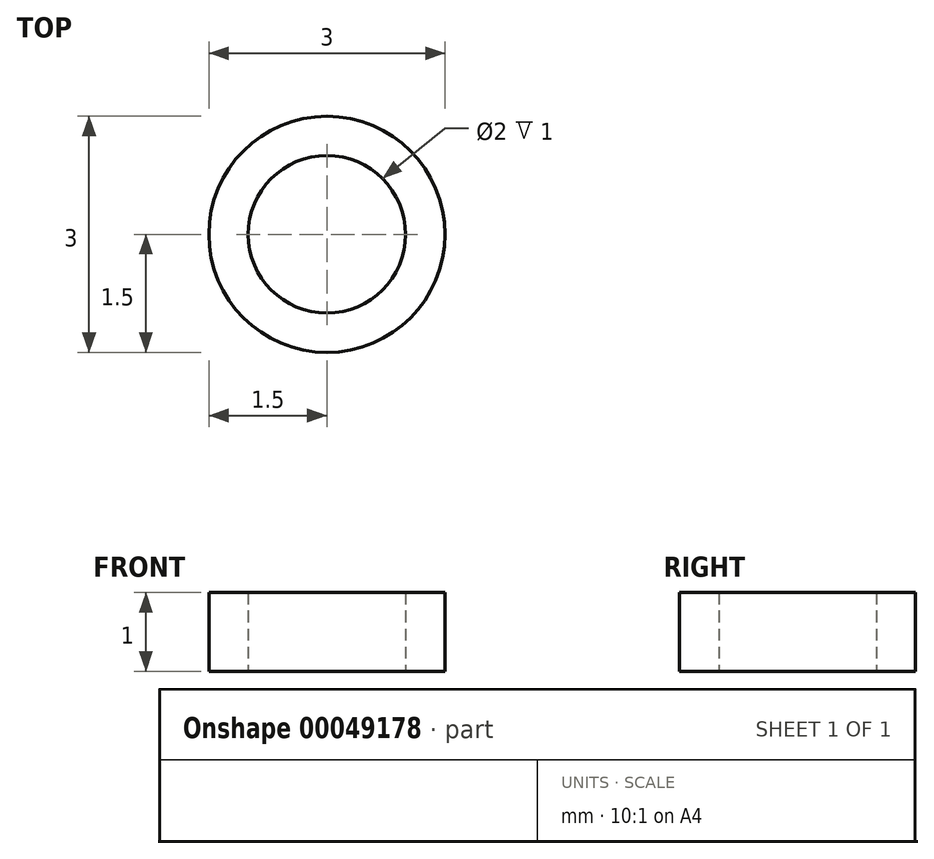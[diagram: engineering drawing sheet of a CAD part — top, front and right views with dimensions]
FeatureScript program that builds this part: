
annotation { "Feature Type Name" : "Feature", "Feature Type Description" : "" }
export const myFeature = defineFeature(function(context is Context, id is Id, definition is map)
    precondition{}
    {
        {
            var Q0;
            Q0=qCreatedBy(makeId("Top.planeOp"),FACE);
            var sketch = newSketch(context, id + "F0", { "sketchPlane" : qUnion([Q0])});
            skCircle(sketch, "E0", {"center": v(0, 0) * mm, "radius": 1 * mm});
            skCircle(sketch, "E1", {"center": v(0, 0) * mm, "radius": 1.5 * mm});
            skSolve(sketch);
        }
        {
            var Q0;
            Q0 = qSketchRegion(id + "F0", true);
            extrude(context, id + "F1", {"entities" : qUnion([Q0]), "depth" : 1 * mm});
        }
    });
